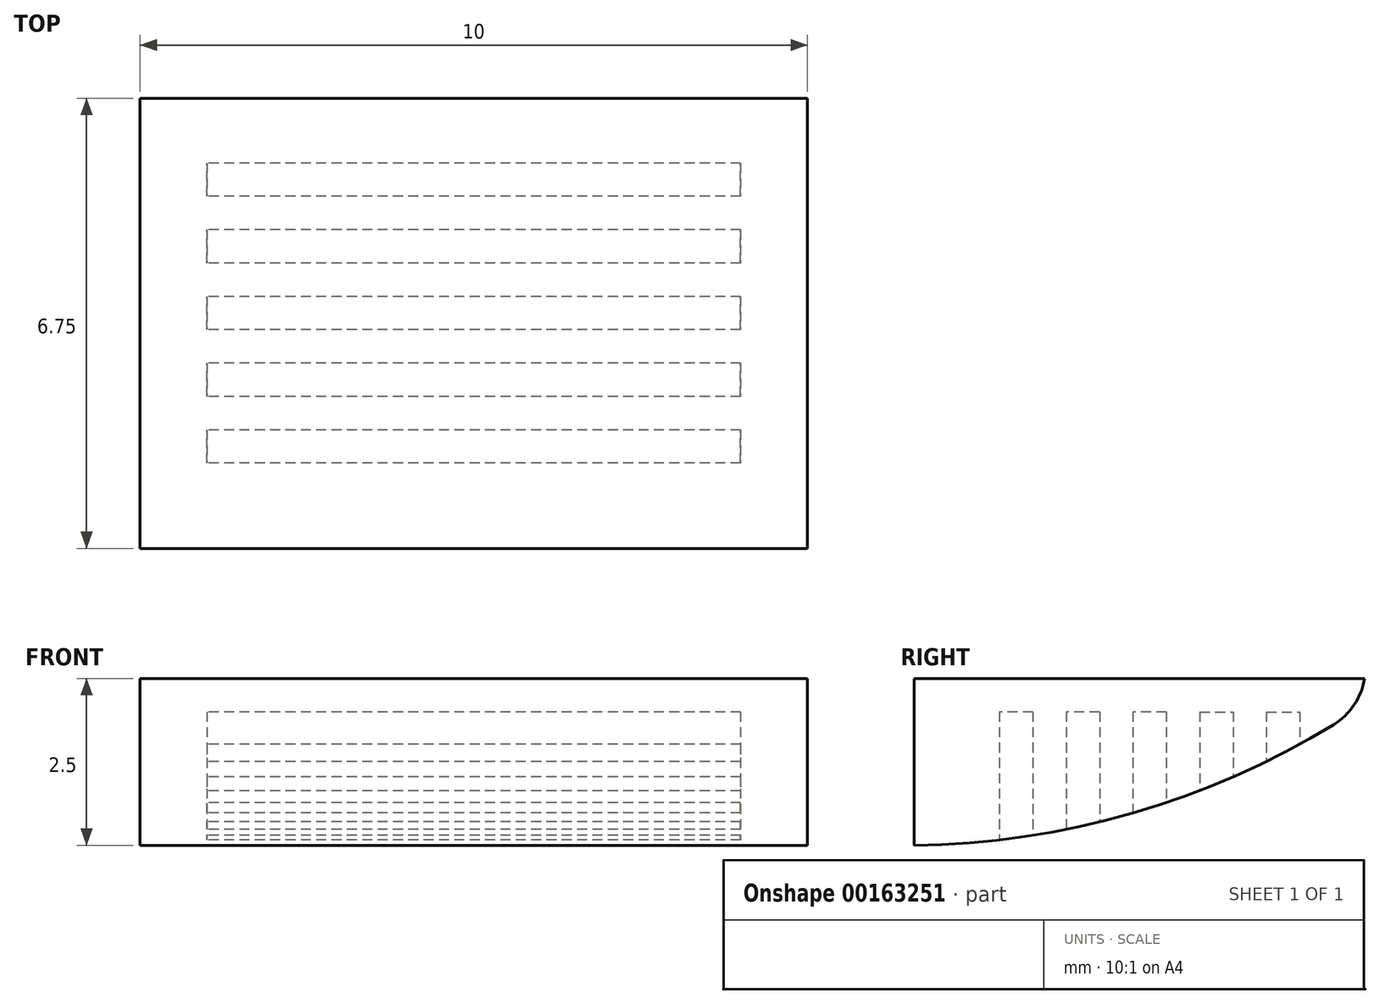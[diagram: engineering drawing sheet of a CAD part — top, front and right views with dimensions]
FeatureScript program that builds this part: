
annotation { "Feature Type Name" : "Feature", "Feature Type Description" : "" }
export const myFeature = defineFeature(function(context is Context, id is Id, definition is map)
    precondition{}
    {
        {
            var Q0;
            Q0=qCreatedBy(makeId("Top.planeOp"),FACE);
            var sketch = newSketch(context, id + "F0", { "sketchPlane" : qUnion([Q0])});
            skLineSegment(sketch, "E0.bottom", {"start": v(0, 0) * mm, "end": v(10, 0) * mm});
            skLineSegment(sketch, "E0.top", {"start": v(0, 7.14) * mm, "end": v(10, 7.14) * mm});
            skLineSegment(sketch, "E0.left", {"start": v(0, 0) * mm, "end": v(0, 7.14) * mm});
            skLineSegment(sketch, "E0.right", {"start": v(10, 0) * mm, "end": v(10, 7.14) * mm});
            skSolve(sketch);
        }
        {
            var Q0;
            Q0 = qSketchRegion(id + "F0", true);
            extrude(context, id + "F1", {"entities" : qUnion([Q0]), "depth" : 2.5 * mm});
        }
        {
            var Q0;
            Q0=makeQuery(id+"F1.opExtrude","SWEPT_FACE",FACE,{"disambiguationData":[OSD([sQuery(id+"F0.wireOp",EDGE,"E0.left")])]});
            var sketch = newSketch(context, id + "F2", { "sketchPlane" : qUnion([Q0])});
            skLineSegment(sketch, "E1", {"start": v(0, 2.25) * mm, "end": v(0, 0) * mm});
            skArc(sketch, "E2", {"start": v(-6.75, 2.1) * mm, "mid": v(-3.53, 0.56) * mm, "end": v(0, 0) * mm});
            skLineSegment(sketch, "E3", {"start": v(-6.75, 2.1) * mm, "end": v(-6.75, 12.27) * mm});
            skLineSegment(sketch, "E4", {"start": v(-6.75, 12.27) * mm, "end": v(-9.83, -2.35) * mm});
            skLineSegment(sketch, "E5", {"start": v(-9.83, -2.35) * mm, "end": v(0, 0) * mm});
            skSolve(sketch);
        }
        {
            var Q0;
            Q0 = qSketchRegion(id + "F2", true);
            extrude(context, id + "F3", {"entities" : qUnion([Q0]), "operationType" : NewBodyOperationType.REMOVE, "endBound" : BoundingType.THROUGH_ALL, "oppositeDirection" : true, "depth" : 25 * mm});
        }
        {
            var Q0;
            Q0=makeQuery(id+"F3.boolean.opBoolean","COPY",EDGE,{"derivedFrom":makeQuery(id+"F3.opExtrude","SWEPT_EDGE",EDGE,{"disambiguationData":[OSD([sQuery(id+"F2.wireOp",EDGE,"E2"),sQuery(id+"F2.wireOp",EDGE,"E3")])]})});
            fillet(context, id + "F4", {"entities" : qUnion([Q0]), "radius" : 1 * mm, "tangentPropagation" : true, "allowEdgeOverflow" : false});
        }
        {
            var Q0;
            Q0=makeQuery(id+"F1.opExtrude","CAP_FACE",FACE,{"disambiguationData":[OSD([sQuery(id+"F0.wireOp",EDGE,"E0.bottom"),sQuery(id+"F0.wireOp",EDGE,"E0.top"),sQuery(id+"F0.wireOp",EDGE,"E0.left"),sQuery(id+"F0.wireOp",EDGE,"E0.right")])],"isStart":false});
            cPlane(context, id + "F5", {"entities" : qUnion([Q0]), "cplaneType" : CPlaneType.OFFSET, "offset" : 2.5 * mm, "oppositeDirection" : true, "width" : 150 * mm, "height" : 150 * mm});
        }
        {
            var Q0;
            Q0=qCreatedBy(id+"F5.planeOp",FACE);
            var sketch = newSketch(context, id + "F6", { "sketchPlane" : qUnion([Q0])});
            skLineSegment(sketch, "E6.bottom", {"start": v(9, 4.28) * mm, "end": v(1, 4.28) * mm});
            skLineSegment(sketch, "E6.top", {"start": v(9, 3.78) * mm, "end": v(1, 3.78) * mm});
            skLineSegment(sketch, "E7.top", {"start": v(9, 3.28) * mm, "end": v(1, 3.28) * mm});
            skLineSegment(sketch, "E7.left", {"start": v(9, 3.78) * mm, "end": v(9, 3.28) * mm});
            skLineSegment(sketch, "E7.right", {"start": v(1, 3.78) * mm, "end": v(1, 3.28) * mm});
            skLineSegment(sketch, "E8.top", {"start": v(9, 2.78) * mm, "end": v(1, 2.78) * mm});
            skLineSegment(sketch, "E9.top", {"start": v(9, 2.28) * mm, "end": v(1, 2.28) * mm});
            skLineSegment(sketch, "E9.left", {"start": v(9, 2.78) * mm, "end": v(9, 2.28) * mm});
            skLineSegment(sketch, "E9.right", {"start": v(1, 2.78) * mm, "end": v(1, 2.28) * mm});
            skLineSegment(sketch, "E10.top", {"start": v(9, 1.78) * mm, "end": v(1, 1.78) * mm});
            skLineSegment(sketch, "E11.top", {"start": v(9, 1.28) * mm, "end": v(1, 1.28) * mm});
            skLineSegment(sketch, "E11.left", {"start": v(9, 1.78) * mm, "end": v(9, 1.28) * mm});
            skLineSegment(sketch, "E11.right", {"start": v(1, 1.78) * mm, "end": v(1, 1.28) * mm});
            skLineSegment(sketch, "E12.top", {"start": v(9, 4.78) * mm, "end": v(1, 4.78) * mm});
            skLineSegment(sketch, "E12.left", {"start": v(9, 4.28) * mm, "end": v(9, 4.78) * mm});
            skLineSegment(sketch, "E12.right", {"start": v(1, 4.28) * mm, "end": v(1, 4.78) * mm});
            skLineSegment(sketch, "E13.bottom", {"start": v(9, 5.28) * mm, "end": v(1, 5.28) * mm});
            skLineSegment(sketch, "E13.top", {"start": v(9, 5.78) * mm, "end": v(1, 5.78) * mm});
            skLineSegment(sketch, "E13.left", {"start": v(9, 5.28) * mm, "end": v(9, 5.78) * mm});
            skLineSegment(sketch, "E13.right", {"start": v(1, 5.28) * mm, "end": v(1, 5.78) * mm});
            skSolve(sketch);
        }
        {
            var Q0;
            Q0 = qSketchRegion(id + "F6", true);
            extrude(context, id + "F7", {"entities" : qUnion([Q0]), "operationType" : NewBodyOperationType.REMOVE, "depth" : 2 * mm});
        }
    });
